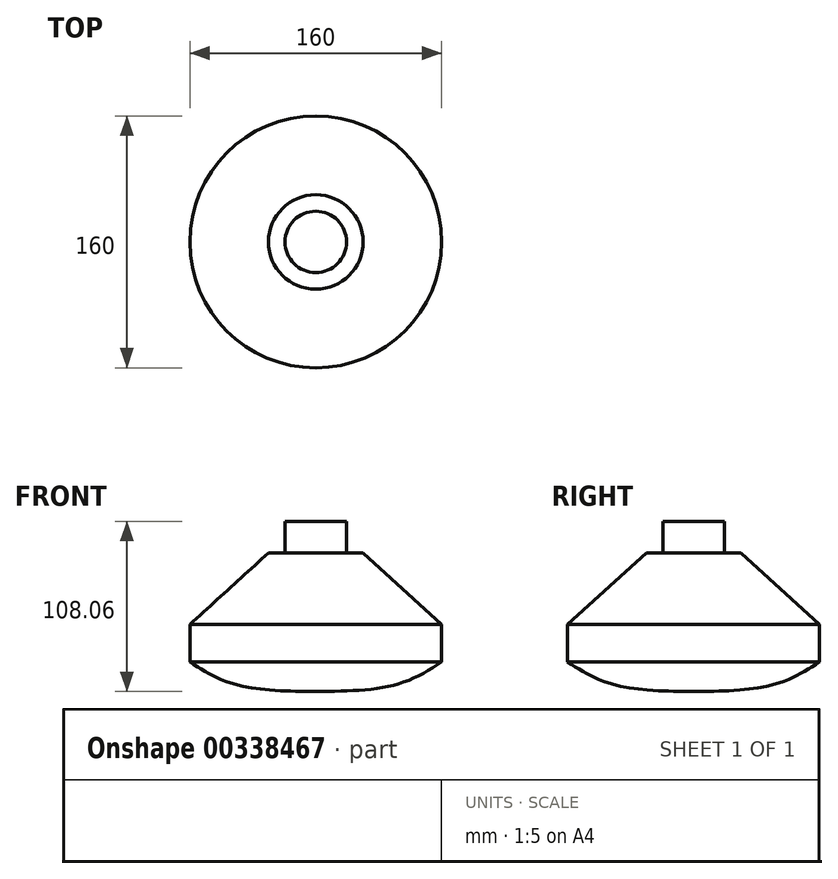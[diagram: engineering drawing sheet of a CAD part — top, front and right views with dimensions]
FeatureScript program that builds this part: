
annotation { "Feature Type Name" : "Feature", "Feature Type Description" : "" }
export const myFeature = defineFeature(function(context is Context, id is Id, definition is map)
    precondition{}
    {
        {
            var Q0;
            Q0=qCreatedBy(makeId("Front.planeOp"),FACE);
            var sketch = newSketch(context, id + "F0", { "sketchPlane" : qUnion([Q0])});
            skLineSegment(sketch, "E0", {"start": v(0, 108.06) * mm, "end": v(19.5, 108.06) * mm});
            skLineSegment(sketch, "E1", {"start": v(19.5, 108.06) * mm, "end": v(19.5, 88.06) * mm});
            skLineSegment(sketch, "E2", {"start": v(19.5, 88.06) * mm, "end": v(30, 88.06) * mm});
            skLineSegment(sketch, "E3", {"start": v(80, 42.55) * mm, "end": v(30, 88.06) * mm});
            skLineSegment(sketch, "E4", {"start": v(0, -1.94) * mm, "end": v(0, 108.06) * mm});
            skLineSegment(sketch, "E5", {"start": v(80, 42.55) * mm, "end": v(80, 18.75) * mm});
            skFitSpline(sketch, "E6", {"points": [v(80, 18.75) * mm, v(58.39, 6.9) * mm, v(32.48, 1.22) * mm, v(0, 0) * mm], "startDerivative": vector(-66.72, -42.13) * mm, "endDerivative": vector(-92.28, -0.87) * mm});
            skLineSegment(sketch, "E7", {"start": v(0, 108.06) * mm, "end": v(0, 0) * mm, "construction": true});
            skLineSegment(sketch, "E8", {"start": v(0, 108.06) * mm, "end": v(0, -1.94) * mm, "construction": true});
            skSolve(sketch);
        }
        {
            var Q0;
            Q0 = qSketchRegion(id + "F0", true);
            var Q1;
            Q1=sQuery(id+"F0.wireOp",EDGE,"E4");
            revolve(context, id + "F1", {"entities" : qUnion([Q0]), "axis" : qUnion([Q1]), "revolveType" : RevolveType.FULL});
        }
    });
